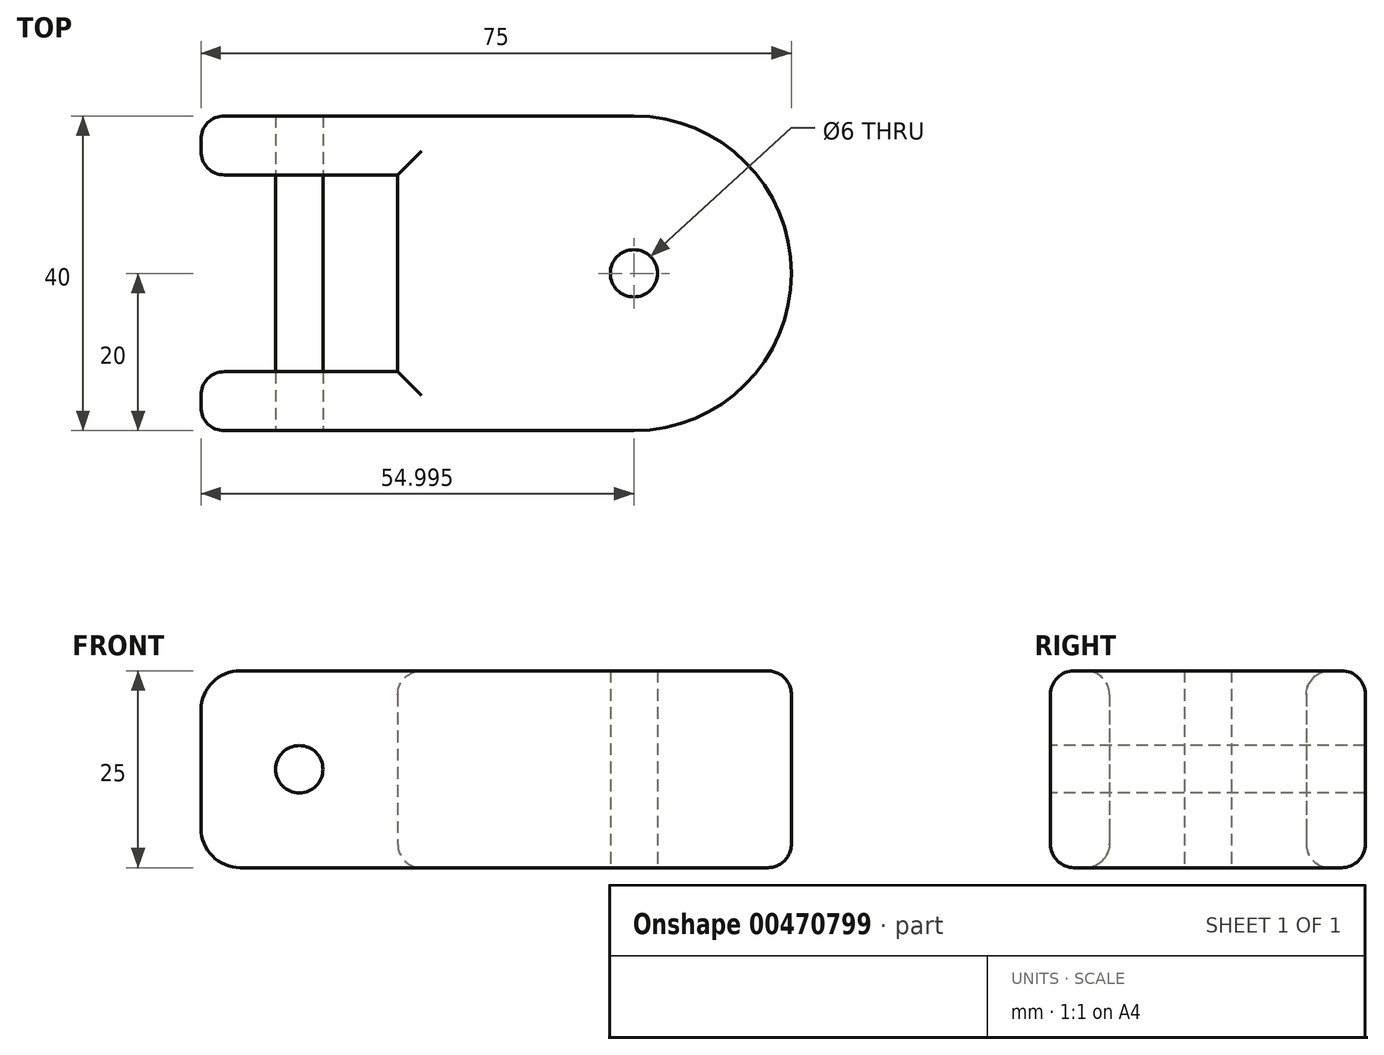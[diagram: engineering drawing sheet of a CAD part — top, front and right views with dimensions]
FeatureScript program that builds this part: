
annotation { "Feature Type Name" : "Feature", "Feature Type Description" : "" }
export const myFeature = defineFeature(function(context is Context, id is Id, definition is map)
    precondition{}
    {
        {
            var Q0;
            Q0=qCreatedBy(makeId("Top.planeOp"),FACE);
            var sketch = newSketch(context, id + "F0", { "sketchPlane" : qUnion([Q0])});
            skLineSegment(sketch, "E0.bottom", {"start": v(6.4, -20) * mm, "end": v(-68.6, -20) * mm});
            skLineSegment(sketch, "E0.top", {"start": v(6.4, 20) * mm, "end": v(-68.6, 20) * mm});
            skLineSegment(sketch, "E0.left", {"start": v(6.4, -20) * mm, "end": v(6.4, 20) * mm});
            skLineSegment(sketch, "E0.right", {"start": v(-68.6, -20) * mm, "end": v(-68.6, 20) * mm});
            skPoint(sketch, "E0.middle", {"position": v(-31.1, 0) * mm});
            skCircle(sketch, "E1", {"center": v(-13.6, 0) * mm, "radius": 3 * mm});
            skCircle(sketch, "E2", {"center": v(-13.6, 0) * mm, "radius": 20 * mm});
            skLineSegment(sketch, "E3.bottom", {"start": v(-43.6, -12.5) * mm, "end": v(-68.6, -12.5) * mm});
            skLineSegment(sketch, "E3.top", {"start": v(-43.6, 12.5) * mm, "end": v(-68.6, 12.5) * mm});
            skLineSegment(sketch, "E3.left", {"start": v(-43.6, -12.5) * mm, "end": v(-43.6, 12.5) * mm});
            skLineSegment(sketch, "E3.right", {"start": v(-68.6, -12.5) * mm, "end": v(-68.6, 12.5) * mm});
            skPoint(sketch, "E3.middle", {"position": v(-56.1, 0) * mm});
            skSolve(sketch);
        }
        {
            var Q0;
            {var subQ9=sQuery(id+"F0.wireOp",EDGE,"E3.bottom");Q0=makeQuery(id+"F0.imprint","IMPRINT",FACE,{"disambiguationData":[TD([[makeQuery(id+"F0.imprint","IMPRINT",EDGE,{"derivedFrom":subQ9}),1.0]])]});}
            var Q1;
            Q1=makeQuery(id+"F0.imprint","IMPRINT",FACE,{"disambiguationData":[TD([[makeQuery(id+"F0.imprint","IMPRINT",EDGE,{"derivedFrom":sQuery(id+"F0.wireOp",EDGE,"E1")}),-1.0]])]});
            extrude(context, id + "F1", {"entities" : qUnion([Q0, Q1]), "endBound" : BoundingType.SYMMETRIC, "depth" : 25 * mm});
        }
        {
            var Q0;
            Q0=makeQuery(id+"F1.opExtrude","SWEPT_FACE",FACE,{"disambiguationData":[OSD([sQuery(id+"F0.wireOp",EDGE,"E0.bottom")])]});
            var sketch = newSketch(context, id + "F2", { "sketchPlane" : qUnion([Q0])});
            skCircle(sketch, "E4", {"center": v(-56.1, 0) * mm, "radius": 3 * mm});
            skSolve(sketch);
        }
        {
            var Q0;
            Q0=makeQuery(id+"F2.imprint","IMPRINT",FACE,{"disambiguationData":[TD([[makeQuery(id+"F2.imprint","IMPRINT",EDGE,{"derivedFrom":sQuery(id+"F2.wireOp",EDGE,"E4")}),1.0]])]});
            var Q1;
            Q1=sQuery(id+"F2.wireOp",EDGE,"E4");
            var Q2;
            Q2=makeQuery(id+"F1.opExtrude","SWEPT_FACE",FACE,{"disambiguationData":[OSD([sQuery(id+"F0.wireOp",EDGE,"E0.top")])]});
            extrude(context, id + "F3", {"entities" : qUnion([Q0]), "surfaceEntities" : qUnion([Q1]), "endBound" : BoundingType.UP_TO_SURFACE, "oppositeDirection" : true, "endBoundEntityFace" : qUnion([Q2]), "depth" : 25 * mm});
        }
        {
            var Q0;
            Q0=makeQuery(id+"F1.opExtrude","CAP_EDGE",EDGE,{"disambiguationData":[OSD([sQuery(id+"F0.wireOp",EDGE,"E0.top")])],"isStart":false});
            var Q1;
            Q1=makeQuery(id+"F1.opExtrude","CAP_EDGE",EDGE,{"disambiguationData":[OSD([sQuery(id+"F0.wireOp",EDGE,"E3.left")])],"isStart":false});
            var Q2;
            Q2=makeQuery(id+"F1.opExtrude","CAP_EDGE",EDGE,{"disambiguationData":[OSD([sQuery(id+"F0.wireOp",EDGE,"E3.top")])],"isStart":false});
            var Q3;
            Q3=makeQuery(id+"F1.opExtrude","CAP_EDGE",EDGE,{"disambiguationData":[OSD([sQuery(id+"F0.wireOp",EDGE,"E3.bottom")])],"isStart":false});
            var Q4;
            Q4=makeQuery(id+"F1.opExtrude","CAP_EDGE",EDGE,{"disambiguationData":[OSD([sQuery(id+"F0.wireOp",EDGE,"E2")])],"isStart":true});
            var Q5;
            Q5=makeQuery(id+"F1.opExtrude","CAP_EDGE",EDGE,{"disambiguationData":[OSD([sQuery(id+"F0.wireOp",EDGE,"E3.left")])],"isStart":true});
            var Q6;
            Q6=makeQuery(id+"F1.opExtrude","SWEPT_EDGE",EDGE,{"disambiguationData":[OSD([sQuery(id+"F0.wireOp",EDGE,"E0.right"),sQuery(id+"F0.wireOp",EDGE,"E3.bottom"),sQuery(id+"F0.wireOp",EDGE,"E3.right")])]});
            var Q7;
            Q7=makeQuery(id+"F1.opExtrude","SWEPT_EDGE",EDGE,{"disambiguationData":[OSD([sQuery(id+"F0.wireOp",EDGE,"E0.right"),sQuery(id+"F0.wireOp",EDGE,"E3.top"),sQuery(id+"F0.wireOp",EDGE,"E3.right")])]});
            var Q8;
            Q8=makeQuery(id+"F1.opExtrude","CAP_EDGE",EDGE,{"disambiguationData":[OSD([sQuery(id+"F0.wireOp",EDGE,"E3.top")])],"isStart":true});
            var Q9;
            Q9=makeQuery(id+"F1.opExtrude","CAP_EDGE",EDGE,{"disambiguationData":[OSD([sQuery(id+"F0.wireOp",EDGE,"E3.bottom")])],"isStart":true});
            var Q10;
            Q10=makeQuery(id+"F1.opExtrude","SWEPT_EDGE",EDGE,{"disambiguationData":[OSD([sQuery(id+"F0.wireOp",EDGE,"E0.bottom"),sQuery(id+"F0.wireOp",EDGE,"E0.right")])]});
            var Q11;
            Q11=makeQuery(id+"F1.opExtrude","SWEPT_EDGE",EDGE,{"disambiguationData":[OSD([sQuery(id+"F0.wireOp",EDGE,"E0.top"),sQuery(id+"F0.wireOp",EDGE,"E0.right")])]});
            fillet(context, id + "F4", {"entities" : qUnion([Q0, Q1, Q2, Q3, Q4, Q5, Q6, Q7, Q8, Q9, Q10, Q11]), "radius" : 3 * mm, "tangentPropagation" : true, "allowEdgeOverflow" : false});
        }
        {
            var Q0;
            {var subQ0=sQuery(id+"F0.wireOp",EDGE,"E0.right");Q0=makeQuery(id+"F1.opExtrude","CAP_EDGE",EDGE,{"disambiguationData":[OSD([subQ0]),TDD([makeQuery(id+"F0.imprint","IMPRINT",EDGE,{"disambiguationData":[TD([[makeQuery(id+"F0.imprint","INTERSECT",VERTEX,{"derivedFrom":[sQuery(id+"F0.wireOp",EDGE,"E0.top"),subQ0]}),1.0]])],"derivedFrom":subQ0})])],"isStart":false});}
            var Q1;
            {var subQ0=sQuery(id+"F0.wireOp",EDGE,"E0.right");Q1=makeQuery(id+"F1.opExtrude","CAP_EDGE",EDGE,{"disambiguationData":[OSD([subQ0]),TDD([makeQuery(id+"F0.imprint","IMPRINT",EDGE,{"disambiguationData":[TD([[makeQuery(id+"F0.imprint","INTERSECT",VERTEX,{"derivedFrom":[sQuery(id+"F0.wireOp",EDGE,"E0.top"),subQ0]}),1.0]])],"derivedFrom":subQ0})])],"isStart":true});}
            var Q2;
            {var subQ0=sQuery(id+"F0.wireOp",EDGE,"E0.right");Q2=makeQuery(id+"F1.opExtrude","CAP_EDGE",EDGE,{"disambiguationData":[OSD([subQ0]),TDD([makeQuery(id+"F0.imprint","IMPRINT",EDGE,{"disambiguationData":[TD([[makeQuery(id+"F0.imprint","INTERSECT",VERTEX,{"derivedFrom":[sQuery(id+"F0.wireOp",EDGE,"E0.bottom"),subQ0]}),-1.0]])],"derivedFrom":subQ0})])],"isStart":true});}
            var Q3;
            {var subQ0=sQuery(id+"F0.wireOp",EDGE,"E0.right");Q3=makeQuery(id+"F1.opExtrude","CAP_EDGE",EDGE,{"disambiguationData":[OSD([subQ0]),TDD([makeQuery(id+"F0.imprint","IMPRINT",EDGE,{"disambiguationData":[TD([[makeQuery(id+"F0.imprint","INTERSECT",VERTEX,{"derivedFrom":[sQuery(id+"F0.wireOp",EDGE,"E0.bottom"),subQ0]}),-1.0]])],"derivedFrom":subQ0})])],"isStart":false});}
            fillet(context, id + "F5", {"entities" : qUnion([Q0, Q1, Q2, Q3]), "radius" : 5 * mm, "tangentPropagation" : true, "allowEdgeOverflow" : false});
        }
    });
